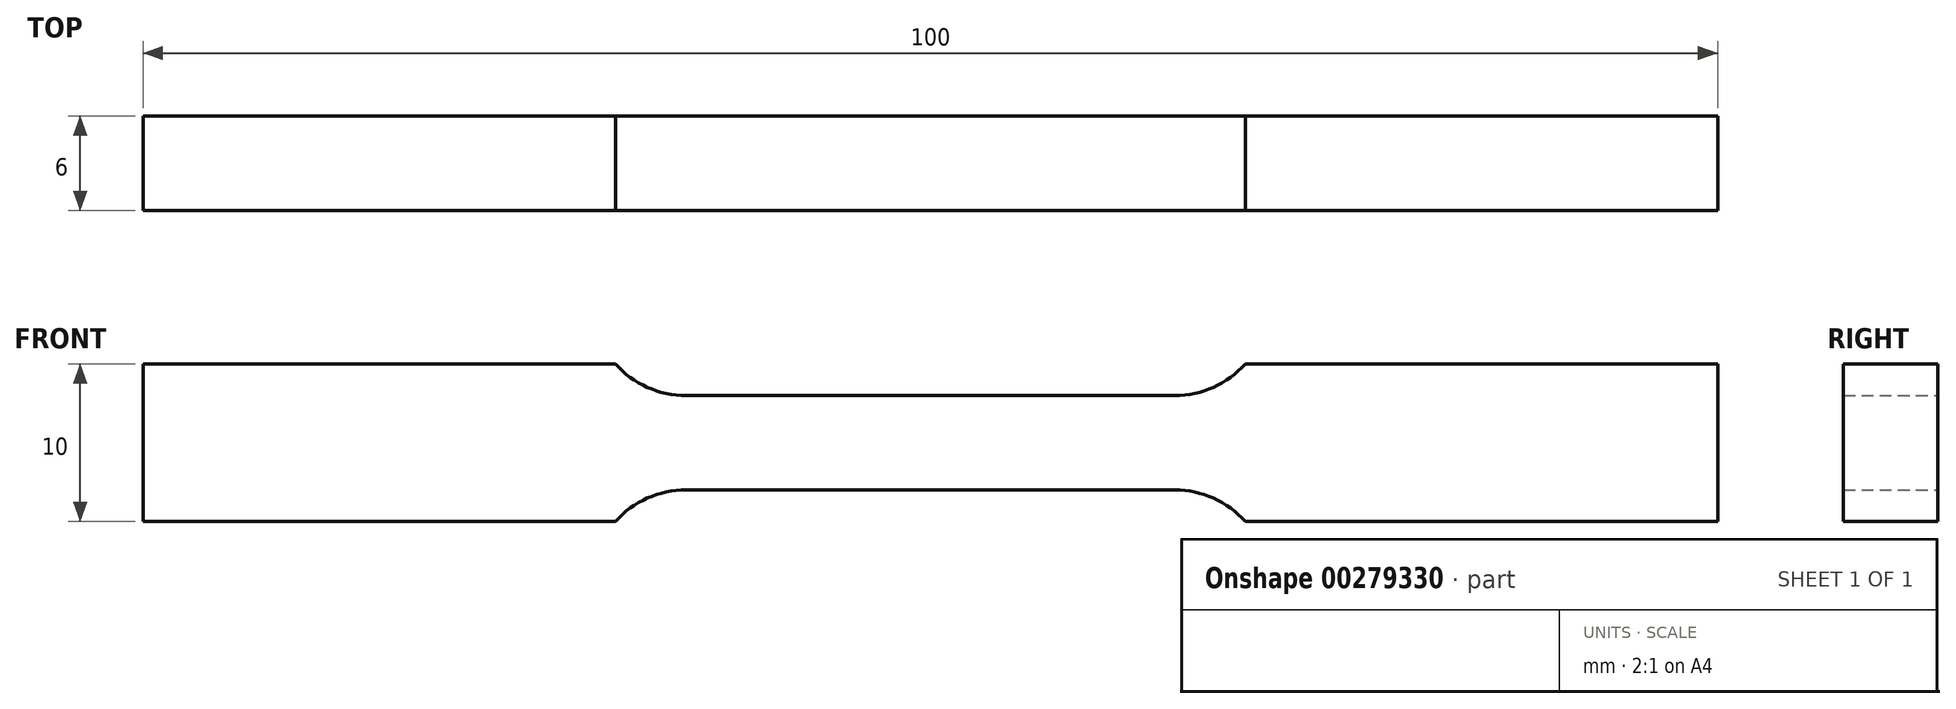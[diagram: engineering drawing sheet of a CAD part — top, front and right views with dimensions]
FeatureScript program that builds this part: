
annotation { "Feature Type Name" : "Feature", "Feature Type Description" : "" }
export const myFeature = defineFeature(function(context is Context, id is Id, definition is map)
    precondition{}
    {
        {
            var Q0;
            Q0=qCreatedBy(makeId("Front.planeOp"),FACE);
            var sketch = newSketch(context, id + "F0", { "sketchPlane" : qUnion([Q0])});
            skLineSegment(sketch, "E0", {"start": v(0, 3) * mm, "end": v(15.53, 3) * mm});
            skArc(sketch, "E1", {"start": v(15.53, 3) * mm, "mid": v(17.98, 3.52) * mm, "end": v(20, 5) * mm});
            skLineSegment(sketch, "E2", {"start": v(20, 5) * mm, "end": v(50, 5) * mm});
            skLineSegment(sketch, "E3", {"start": v(50, 5) * mm, "end": v(50, 0) * mm});
            skLineSegment(sketch, "E4.MirrorCS", {"start": v(0, -3) * mm, "end": v(15.53, -3) * mm});
            skLineSegment(sketch, "E5.MirrorCS", {"start": v(20, -5) * mm, "end": v(50, -5) * mm});
            skArc(sketch, "E6.MirrorCS", {"start": v(15.53, -3) * mm, "mid": v(17.98, -3.52) * mm, "end": v(20, -5) * mm});
            skLineSegment(sketch, "E7.MirrorCS", {"start": v(50, -5) * mm, "end": v(50, 0) * mm});
            skLineSegment(sketch, "E8.MirrorCS", {"start": v(-50, -5) * mm, "end": v(-50, 0) * mm});
            skArc(sketch, "E9.MirrorCS", {"start": v(-15.53, -3) * mm, "mid": v(-17.98, -3.52) * mm, "end": v(-20, -5) * mm});
            skArc(sketch, "E10.MirrorCS", {"start": v(-15.53, 3) * mm, "mid": v(-17.98, 3.52) * mm, "end": v(-20, 5) * mm});
            skLineSegment(sketch, "E11.MirrorCS", {"start": v(-20, 5) * mm, "end": v(-50, 5) * mm});
            skLineSegment(sketch, "E12.MirrorCS", {"start": v(-20, -5) * mm, "end": v(-50, -5) * mm});
            skLineSegment(sketch, "E13.MirrorCS", {"start": v(0, -3) * mm, "end": v(-15.53, -3) * mm});
            skLineSegment(sketch, "E14.MirrorCS", {"start": v(-50, 5) * mm, "end": v(-50, 0) * mm});
            skLineSegment(sketch, "E15.MirrorCS", {"start": v(0, 3) * mm, "end": v(-15.53, 3) * mm});
            skSolve(sketch);
        }
        {
            var Q0;
            Q0 = qSketchRegion(id + "F0", true);
            extrude(context, id + "F1", {"entities" : qUnion([Q0]), "endBound" : BoundingType.SYMMETRIC, "depth" : 6 * mm});
        }
    });
